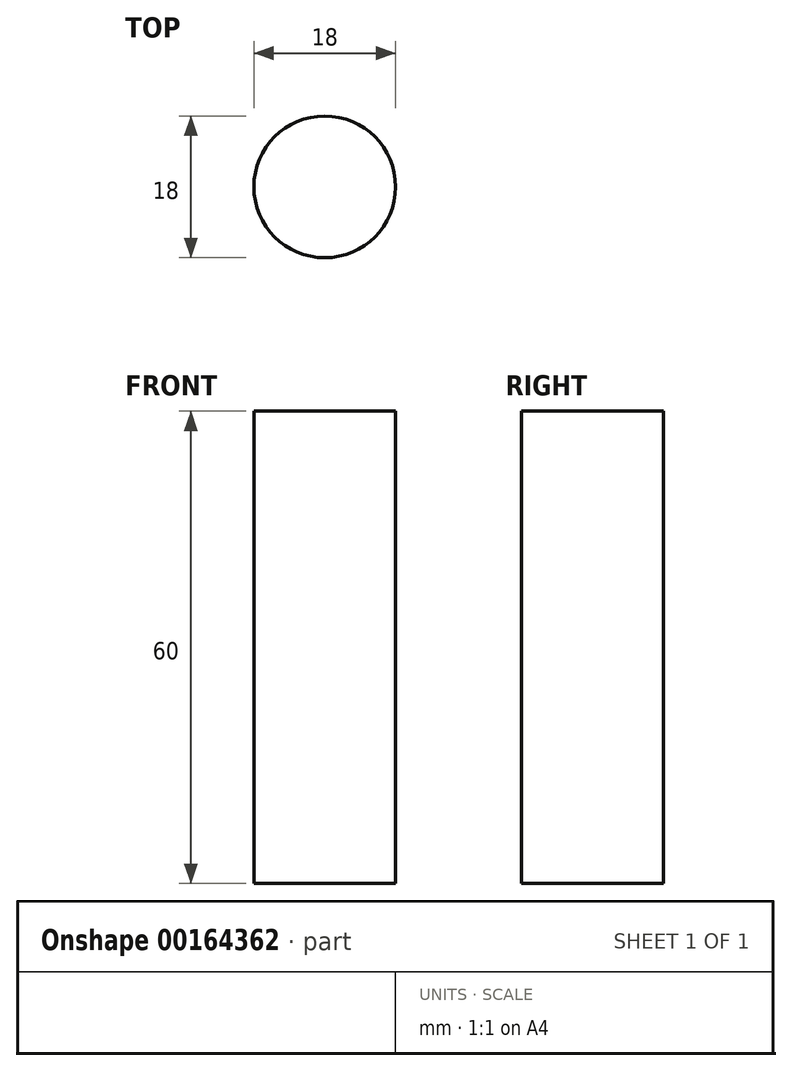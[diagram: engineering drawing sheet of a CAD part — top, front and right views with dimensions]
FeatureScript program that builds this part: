
annotation { "Feature Type Name" : "Feature", "Feature Type Description" : "" }
export const myFeature = defineFeature(function(context is Context, id is Id, definition is map)
    precondition{}
    {
        {
            var Q0;
            Q0=qCreatedBy(makeId("Top.planeOp"),FACE);
            var sketch = newSketch(context, id + "F0", { "sketchPlane" : qUnion([Q0])});
            skCircle(sketch, "E0", {"center": v(0, 0) * mm, "radius": 9 * mm});
            skSolve(sketch);
        }
        {
            var Q0;
            Q0=qSketchRegion(id+"F0",true);
            extrude(context, id + "F1", {"entities" : qUnion([Q0]), "depth" : 60 * mm});
        }
    });
